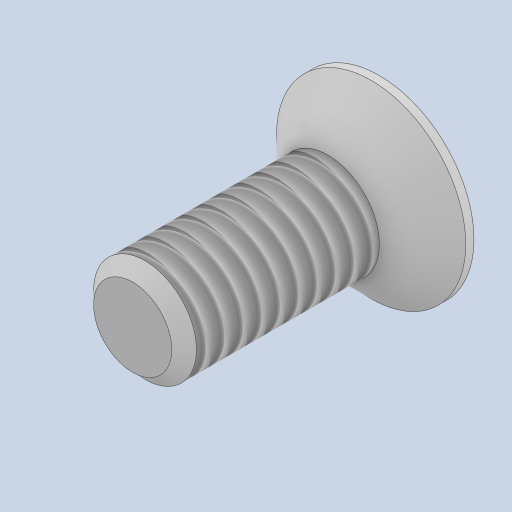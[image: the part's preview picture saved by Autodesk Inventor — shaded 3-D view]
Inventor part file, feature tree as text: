
AUTODESK INVENTOR PART (.ipt)
format: ipt  version: 2023 (Build 270158000, 158)  size: 180,224 bytes
history: native  units: in
note: dims shown in document units (in); Inventor stores cm internally (conversion verified against a paired STEP export)
features: sketch x2, other x1, revolve x1, extrude x1, thread x1
ambient origin geometry x8: Origin, YZ Plane, XZ Plane, XY Plane, X Axis, Y Axis, Z Axis, Center Point
bodies: Body1 (feature_tree)
feature tree (6):
  other  "ソリッド1"
  revolve  "回転1"
  extrude  "押し出し1"  Depth=0.2362in
  thread  "ねじ1"
  sketch  "スケッチ1"
  sketch  "スケッチ2"
